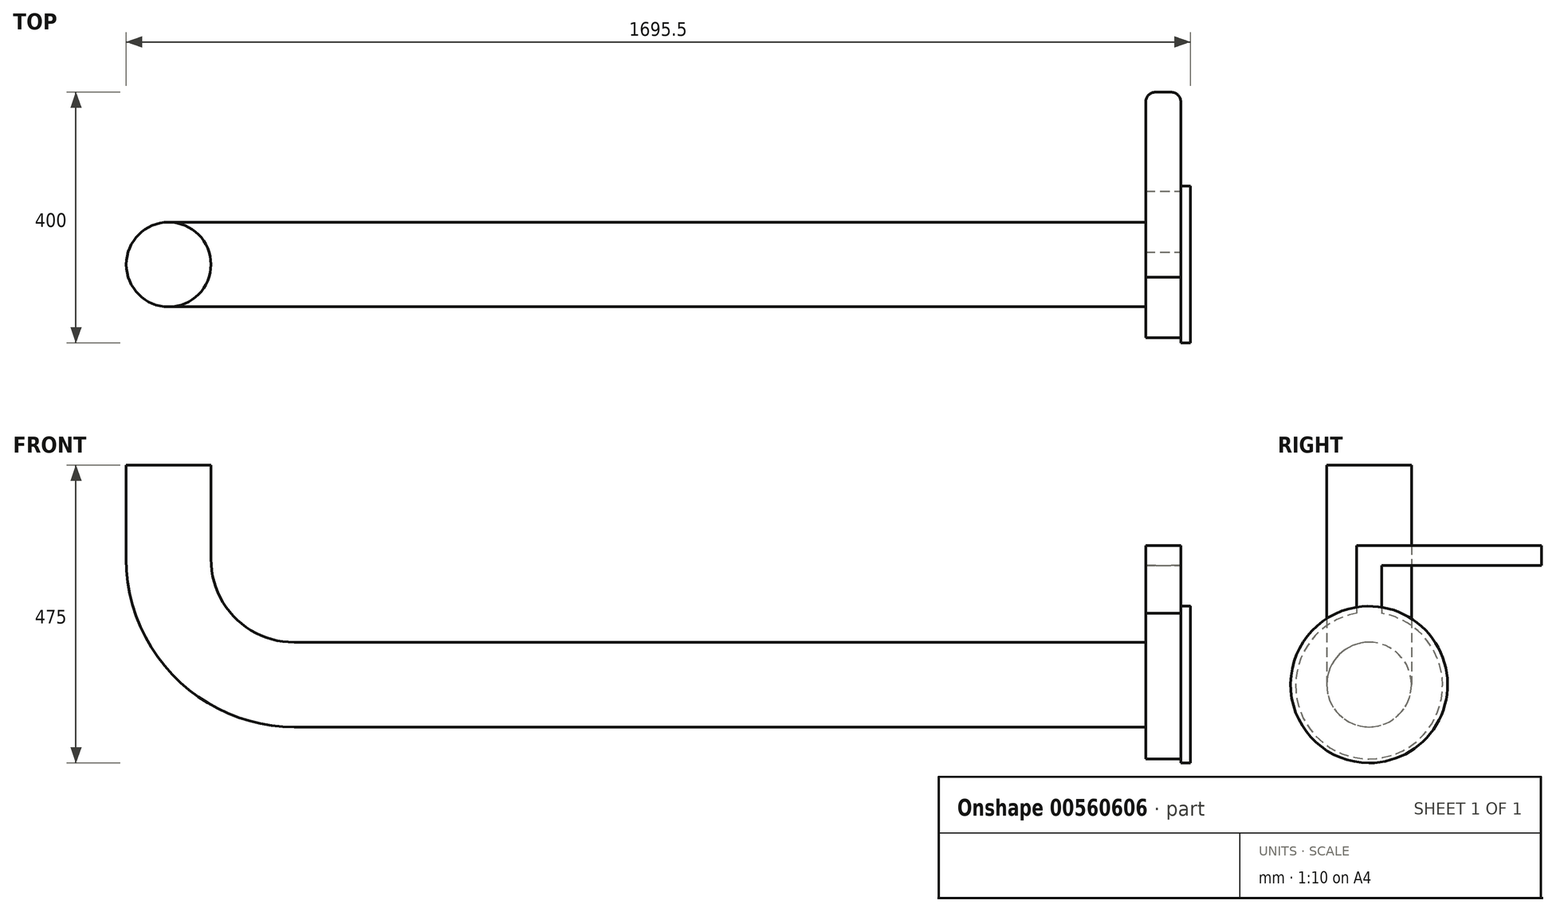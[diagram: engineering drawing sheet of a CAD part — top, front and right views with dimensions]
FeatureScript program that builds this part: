
annotation { "Feature Type Name" : "Feature", "Feature Type Description" : "" }
export const myFeature = defineFeature(function(context is Context, id is Id, definition is map)
    precondition{}
    {
        {
            var Q0;
            Q0=qCreatedBy(makeId("Top.planeOp"),FACE);
            var sketch = newSketch(context, id + "F0", { "sketchPlane" : qUnion([Q0])});
            skCircle(sketch, "E0", {"center": v(0, 0) * mm, "radius": 67.5 * mm});
            skSolve(sketch);
        }
        {
            var Q0;
            Q0=qCreatedBy(makeId("Front.planeOp"),FACE);
            var sketch = newSketch(context, id + "F1", { "sketchPlane" : qUnion([Q0])});
            skLineSegment(sketch, "E1", {"start": v(0, 0) * mm, "end": v(0, -150) * mm});
            skLineSegment(sketch, "E2", {"start": v(200, -350) * mm, "end": v(1613, -350) * mm});
            skPoint(sketch, "E3.visualSharp", {"position": v(0, -350) * mm});
            skArc(sketch, "E3.filletArc", {"start": v(0, -150) * mm, "mid": v(58.58, -291.42) * mm, "end": v(200, -350) * mm});
            skSolve(sketch);
        }
        {
            var Q0;
            Q0=qCreatedBy(makeId("Right.planeOp"),FACE);
            cPlane(context, id + "F2", {"entities" : qUnion([Q0]), "cplaneType" : CPlaneType.OFFSET, "offset" : 1613 * mm, "width" : 150 * mm, "height" : 150 * mm});
        }
        {
            var Q0;
            Q0=qCreatedBy(id+"F2.planeOp",FACE);
            var sketch = newSketch(context, id + "F3", { "sketchPlane" : qUnion([Q0])});
            skPoint(sketch, "E4.0", {"position": v(0, -350) * mm});
            skCircle(sketch, "E5", {"center": v(0, -350) * mm, "radius": 125 * mm});
            skSolve(sketch);
        }
        {
            var Q0;
            Q0=makeQuery(id+"F3.imprint","IMPRINT",FACE,{"disambiguationData":[TD([[makeQuery(id+"F3.imprint","IMPRINT",EDGE,{"derivedFrom":sQuery(id+"F3.wireOp",EDGE,"E5")}),1.0]])]});
            extrude(context, id + "F4", {"entities" : qUnion([Q0]), "depth" : 15 * mm, "offsetDistance" : 25 * mm});
        }
        {
            var Q0;
            Q0=makeQuery(id+"F0.imprint","IMPRINT",FACE,{"disambiguationData":[TD([[makeQuery(id+"F0.imprint","IMPRINT",EDGE,{"derivedFrom":sQuery(id+"F0.wireOp",EDGE,"E0")}),1.0]])]});
            var Q1;
            Q1=sQuery(id+"F1.wireOp",EDGE,"E1");
            var Q2;
            Q2=sQuery(id+"F1.wireOp",EDGE,"E3.filletArc");
            var Q3;
            Q3=sQuery(id+"F1.wireOp",EDGE,"E2");
            sweep(context, id + "F5", {"operationType" : NewBodyOperationType.ADD, "profiles" : qUnion([Q0]), "path" : qUnion([Q1, Q2, Q3])});
        }
        {
            var Q0;
            Q0=qCreatedBy(id+"F2.planeOp",FACE);
            var sketch = newSketch(context, id + "F6", { "sketchPlane" : qUnion([Q0])});
            skCircle(sketch, "E6", {"center": v(0, -1239.55) * mm, "radius": 98.5 * mm});
            skCircle(sketch, "E7", {"center": v(0, -351.44) * mm, "radius": 117 * mm});
            skSolve(sketch);
        }
        {
            var Q0;
            Q0=makeQuery(id+"F6.imprint","IMPRINT",FACE,{"disambiguationData":[TD([[makeQuery(id+"F6.imprint","IMPRINT",EDGE,{"derivedFrom":sQuery(id+"F6.wireOp",EDGE,"E7")}),1.0]])]});
            extrude(context, id + "F7", {"entities" : qUnion([Q0]), "operationType" : NewBodyOperationType.ADD, "oppositeDirection" : true, "depth" : 56 * mm, "offsetDistance" : 25 * mm});
        }
        {
            var Q0;
            Q0=qCreatedBy(id+"F2.planeOp",FACE);
            var sketch = newSketch(context, id + "F8", { "sketchPlane" : qUnion([Q0])});
            skLineSegment(sketch, "E8.bottom", {"start": v(-20, -128) * mm, "end": v(20, -128) * mm});
            skLineSegment(sketch, "E8.top", {"start": v(-20, -323.04) * mm, "end": v(20, -323.04) * mm});
            skLineSegment(sketch, "E8.left", {"start": v(-20, -128) * mm, "end": v(-20, -323.04) * mm});
            skLineSegment(sketch, "E8.right", {"start": v(20, -128) * mm, "end": v(20, -323.04) * mm});
            skSolve(sketch);
        }
        {
            var Q0;
            Q0=makeQuery(id+"F8.imprint","IMPRINT",FACE,{"disambiguationData":[TD([[makeQuery(id+"F8.imprint","IMPRINT",EDGE,{"derivedFrom":sQuery(id+"F8.wireOp",EDGE,"E8.bottom")}),-1.0]])]});
            extrude(context, id + "F9", {"entities" : qUnion([Q0]), "operationType" : NewBodyOperationType.ADD, "oppositeDirection" : true, "depth" : 56 * mm, "offsetDistance" : 25 * mm});
        }
        {
            var Q0;
            Q0=makeQuery(id+"F9.opExtrude","SWEPT_FACE",FACE,{"disambiguationData":[OSD([sQuery(id+"F8.wireOp",EDGE,"E8.bottom")])]});
            var sketch = newSketch(context, id + "F10", { "sketchPlane" : qUnion([Q0])});
            skLineSegment(sketch, "E9.bottom", {"start": v(1557, -20) * mm, "end": v(1613, -20) * mm});
            skLineSegment(sketch, "E9.top", {"start": v(1572.84, 275) * mm, "end": v(1597.16, 275) * mm});
            skLineSegment(sketch, "E9.left", {"start": v(1557, -20) * mm, "end": v(1557, 259.16) * mm});
            skLineSegment(sketch, "E9.right", {"start": v(1613, -20) * mm, "end": v(1613, 259.16) * mm});
            skPoint(sketch, "E10.visualSharp", {"position": v(1557, 275) * mm});
            skArc(sketch, "E10.filletArc", {"start": v(1572.84, 275) * mm, "mid": v(1561.64, 270.36) * mm, "end": v(1557, 259.16) * mm});
            skPoint(sketch, "E11.visualSharp", {"position": v(1613, 275) * mm});
            skArc(sketch, "E11.filletArc", {"start": v(1613, 259.16) * mm, "mid": v(1608.36, 270.36) * mm, "end": v(1597.16, 275) * mm});
            skSolve(sketch);
        }
        {
            var Q0;
            Q0=makeQuery(id+"F10.imprint","IMPRINT",FACE,{"disambiguationData":[TD([[makeQuery(id+"F10.imprint","IMPRINT",EDGE,{"derivedFrom":sQuery(id+"F10.wireOp",EDGE,"E9.top")}),-1.0]])]});
            extrude(context, id + "F11", {"entities" : qUnion([Q0]), "operationType" : NewBodyOperationType.ADD, "oppositeDirection" : true, "depth" : 32 * mm, "offsetDistance" : 25 * mm});
        }
    });
